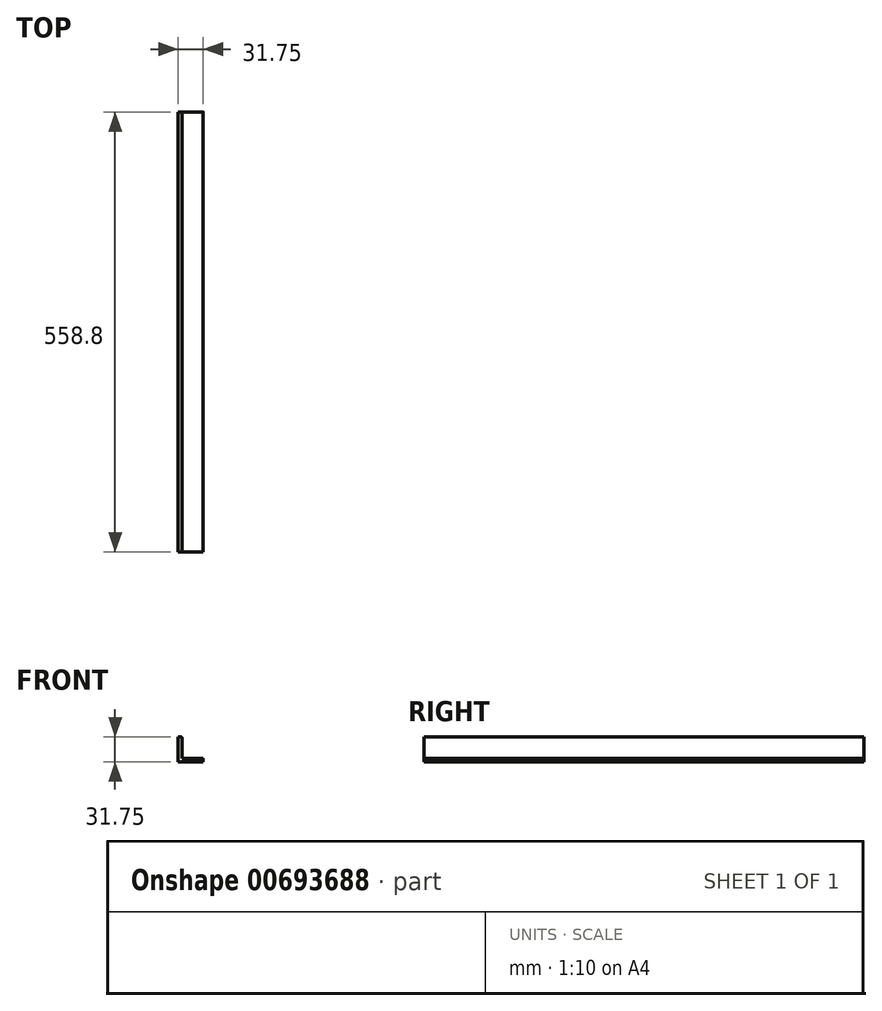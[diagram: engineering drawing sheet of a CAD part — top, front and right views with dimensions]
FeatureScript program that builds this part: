
annotation { "Feature Type Name" : "Feature", "Feature Type Description" : "" }
export const myFeature = defineFeature(function(context is Context, id is Id, definition is map)
    precondition{}
    {
        {
            var Q0;
            Q0=qCreatedBy(makeId("Front.planeOp"),FACE);
            var sketch = newSketch(context, id + "F0", { "sketchPlane" : qUnion([Q0])});
            skLineSegment(sketch, "E0", {"start": v(0, 0) * mm, "end": v(31.75, 0) * mm});
            skLineSegment(sketch, "E1", {"start": v(31.75, 0) * mm, "end": v(31.75, 3.24) * mm});
            skLineSegment(sketch, "E2", {"start": v(30.23, 4.76) * mm, "end": v(4.76, 4.76) * mm});
            skLineSegment(sketch, "E3", {"start": v(4.76, 4.76) * mm, "end": v(4.76, 30.23) * mm});
            skLineSegment(sketch, "E4", {"start": v(3.24, 31.75) * mm, "end": v(0, 31.75) * mm});
            skLineSegment(sketch, "E5", {"start": v(0, 31.75) * mm, "end": v(0, 0) * mm});
            skPoint(sketch, "E6.visualSharp", {"position": v(31.75, 4.76) * mm});
            skArc(sketch, "E6.filletArc", {"start": v(31.75, 3.24) * mm, "mid": v(31.3, 4.32) * mm, "end": v(30.23, 4.76) * mm});
            skPoint(sketch, "E7.visualSharp", {"position": v(4.76, 31.75) * mm});
            skArc(sketch, "E7.filletArc", {"start": v(4.76, 30.23) * mm, "mid": v(4.32, 31.3) * mm, "end": v(3.24, 31.75) * mm});
            skSolve(sketch);
        }
        {
            var Q0;
            Q0=qSketchRegion(id+"F0",true);
            extrude(context, id + "F1", {"entities" : qUnion([Q0]), "endBound" : BoundingType.SYMMETRIC, "depth" : 558.8 * mm, "offsetDistance" : 25.4 * mm});
        }
    });
